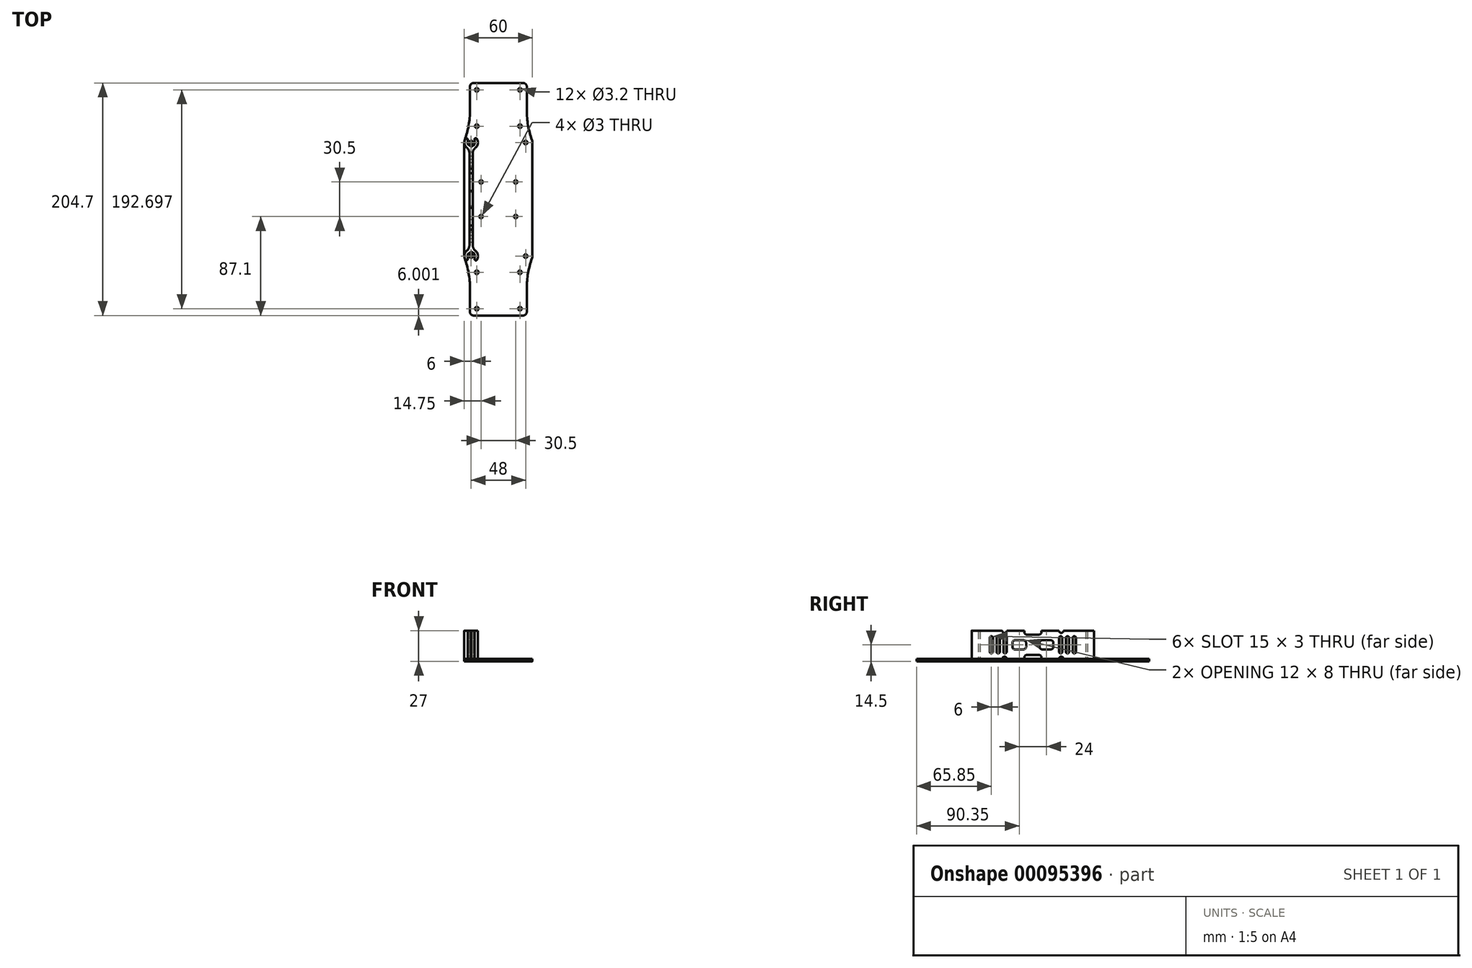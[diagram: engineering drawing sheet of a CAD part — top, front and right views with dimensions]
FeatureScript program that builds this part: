
annotation { "Feature Type Name" : "Feature", "Feature Type Description" : "" }
export const myFeature = defineFeature(function(context is Context, id is Id, definition is map)
    precondition{}
    {
        {
            var Q0;
            Q0=qCreatedBy(makeId("Top.planeOp"),FACE);
            var sketch = newSketch(context, id + "F0", { "sketchPlane" : qUnion([Q0])});
            skLineSegment(sketch, "E0", {"start": v(0, 102.35) * mm, "end": v(-22, 102.35) * mm});
            skLineSegment(sketch, "E1", {"start": v(-25, 99.35) * mm, "end": v(-25, 78.35) * mm});
            skLineSegment(sketch, "E2", {"start": v(-22, -102.35) * mm, "end": v(0, -102.35) * mm});
            skArc(sketch, "E3.filletArc", {"start": v(-22, 102.35) * mm, "mid": v(-24.12, 101.47) * mm, "end": v(-25, 99.35) * mm});
            skArc(sketch, "E4.filletArc", {"start": v(-25, -99.35) * mm, "mid": v(-24.12, -101.47) * mm, "end": v(-22, -102.35) * mm});
            skArc(sketch, "E5.filletArc", {"start": v(-29.64, 52.05) * mm, "mid": v(-29.9, 51.04) * mm, "end": v(-30, 50) * mm});
            skArc(sketch, "E6.MirrorCS", {"start": v(-29.64, -52.05) * mm, "mid": v(-29.9, -51.04) * mm, "end": v(-30, -50) * mm});
            skLineSegment(sketch, "E7.trimOffspring", {"start": v(-25, -78.35) * mm, "end": v(-25, -99.35) * mm});
            skArc(sketch, "E8", {"start": v(-25, -78.35) * mm, "mid": v(-26.17, -65) * mm, "end": v(-29.64, -52.05) * mm});
            skArc(sketch, "E9", {"start": v(-29.64, 52.05) * mm, "mid": v(-26.17, 65) * mm, "end": v(-25, 78.35) * mm});
            skCircle(sketch, "E10", {"center": v(0, 0) * mm, "radius": 125 * mm, "construction": true});
            skLineSegment(sketch, "E11", {"start": v(-95.76, 80.35) * mm, "end": v(95.76, -80.35) * mm, "construction": true});
            skLineSegment(sketch, "E12", {"start": v(95.76, 80.35) * mm, "end": v(-95.76, -80.35) * mm, "construction": true});
            skLineSegment(sketch, "E13", {"start": v(0, 125) * mm, "end": v(0, -125) * mm, "construction": true});
            skLineSegment(sketch, "E14", {"start": v(-95.76, 80.35) * mm, "end": v(95.76, 80.35) * mm, "construction": true});
            skLineSegment(sketch, "E15", {"start": v(-95.76, -80.35) * mm, "end": v(95.76, -80.35) * mm, "construction": true});
            skLineSegment(sketch, "E16", {"start": v(-30, 50) * mm, "end": v(-30, -50) * mm});
            skLineSegment(sketch, "E17.MirrorCS", {"start": v(0, 102.35) * mm, "end": v(22, 102.35) * mm});
            skArc(sketch, "E18.MirrorCS", {"start": v(22, 102.35) * mm, "mid": v(24.12, 101.47) * mm, "end": v(25, 99.35) * mm});
            skLineSegment(sketch, "E19.MirrorCS", {"start": v(25, 99.35) * mm, "end": v(25, 78.35) * mm});
            skArc(sketch, "E20.MirrorCS", {"start": v(29.64, 52.05) * mm, "mid": v(26.17, 65) * mm, "end": v(25, 78.35) * mm});
            skArc(sketch, "E21.MirrorCS", {"start": v(29.64, 52.05) * mm, "mid": v(29.9, 51.04) * mm, "end": v(30, 50) * mm});
            skLineSegment(sketch, "E22.MirrorCS", {"start": v(30, 50) * mm, "end": v(30, -50) * mm});
            skArc(sketch, "E23.MirrorCS", {"start": v(29.64, -52.05) * mm, "mid": v(29.9, -51.04) * mm, "end": v(30, -50) * mm});
            skArc(sketch, "E24.MirrorCS", {"start": v(25, -78.35) * mm, "mid": v(26.17, -65) * mm, "end": v(29.64, -52.05) * mm});
            skArc(sketch, "E25.MirrorCS", {"start": v(25, -99.35) * mm, "mid": v(24.12, -101.47) * mm, "end": v(22, -102.35) * mm});
            skLineSegment(sketch, "E26.MirrorCS", {"start": v(22, -102.35) * mm, "end": v(0, -102.35) * mm});
            skLineSegment(sketch, "E27.MirrorCS", {"start": v(25, -78.35) * mm, "end": v(25, -99.35) * mm});
            skSolve(sketch);
        }
        {
            var Q0;
            Q0=qSketchRegion(id+"F0",true);
            extrude(context, id + "F1", {"entities" : qUnion([Q0]), "oppositeDirection" : true, "depth" : 2 * mm});
        }
        {
            var Q0;
            Q0=makeQuery(id+"F1.opExtrude","CAP_FACE",FACE,{"disambiguationData":[OSD([sQuery(id+"F0.wireOp",EDGE,"E0"),sQuery(id+"F0.wireOp",EDGE,"E1"),sQuery(id+"F0.wireOp",EDGE,"E2"),sQuery(id+"F0.wireOp",EDGE,"E3.filletArc"),sQuery(id+"F0.wireOp",EDGE,"E4.filletArc"),sQuery(id+"F0.wireOp",EDGE,"d22b67ea-32aa-4b1a-bfbd-94ae52c1f5b30.MirrorCS"),sQuery(id+"F0.wireOp",EDGE,"d22b67ea-32aa-4b1a-bfbd-94ae52c1f5b31.MirrorCS"),sQuery(id+"F0.wireOp",EDGE,"d22b67ea-32aa-4b1a-bfbd-94ae52c1f5b32.MirrorCS"),sQuery(id+"F0.wireOp",EDGE,"d22b67ea-32aa-4b1a-bfbd-94ae52c1f5b33.MirrorCS"),sQuery(id+"F0.wireOp",EDGE,"d22b67ea-32aa-4b1a-bfbd-94ae52c1f5b34.MirrorCS")])],"isStart":true});
            var sketch = newSketch(context, id + "F2", { "sketchPlane" : qUnion([Q0])});
            skCircle(sketch, "E28", {"center": v(-19, 96.35) * mm, "radius": 1.6 * mm});
            skCircle(sketch, "E29", {"center": v(-19, 64.35) * mm, "radius": 1.6 * mm});
            skCircle(sketch, "E30", {"center": v(-19, -96.35) * mm, "radius": 1.6 * mm});
            skCircle(sketch, "E31", {"center": v(-19, -64.35) * mm, "radius": 1.6 * mm});
            skCircle(sketch, "E32", {"center": v(-24, -50) * mm, "radius": 1.6 * mm});
            skCircle(sketch, "E33", {"center": v(-24, 50) * mm, "radius": 1.6 * mm});
            skLineSegment(sketch, "E34", {"start": v(-19, 96.35) * mm, "end": v(-19, -96.35) * mm, "construction": true});
            skCircle(sketch, "E35.MirrorC", {"center": v(19, 96.35) * mm, "radius": 1.6 * mm});
            skCircle(sketch, "E36.MirrorC", {"center": v(19, 64.35) * mm, "radius": 1.6 * mm});
            skCircle(sketch, "E37.MirrorC", {"center": v(24, 50) * mm, "radius": 1.6 * mm});
            skCircle(sketch, "E38.MirrorC", {"center": v(24, -50) * mm, "radius": 1.6 * mm});
            skCircle(sketch, "E39.MirrorC", {"center": v(19, -64.35) * mm, "radius": 1.6 * mm});
            skCircle(sketch, "E40.MirrorC", {"center": v(19, -96.35) * mm, "radius": 1.6 * mm});
            skLineSegment(sketch, "E41", {"start": v(-15.25, 15.25) * mm, "end": v(-15.25, -15.25) * mm, "construction": true});
            skPoint(sketch, "E42", {"position": v(-15.25, 0) * mm});
            skLineSegment(sketch, "E43", {"start": v(0, 0) * mm, "end": v(-30, 0) * mm, "construction": true});
            skCircle(sketch, "E44", {"center": v(-15.25, -15.25) * mm, "radius": 1.5 * mm});
            skCircle(sketch, "E45", {"center": v(-15.25, 15.25) * mm, "radius": 1.5 * mm});
            skCircle(sketch, "E46.MirrorC", {"center": v(15.25, 15.25) * mm, "radius": 1.5 * mm});
            skCircle(sketch, "E47.MirrorC", {"center": v(15.25, -15.25) * mm, "radius": 1.5 * mm});
            skSolve(sketch);
        }
        {
            var Q0;
            Q0=qSketchRegion(id+"F2",true);
            extrude(context, id + "F3", {"entities" : qUnion([Q0]), "operationType" : NewBodyOperationType.REMOVE, "endBound" : BoundingType.THROUGH_ALL, "oppositeDirection" : true, "depth" : 25.4 * mm});
        }
        {
            var Q0;
            Q0=qCreatedBy(makeId("Top.planeOp"),FACE);
            var sketch = newSketch(context, id + "F4", { "sketchPlane" : qUnion([Q0])});
            skCircle(sketch, "E48.cCircle", {"center": v(-24, 50) * mm, "radius": 3.1 * mm, "construction": true});
            skLineSegment(sketch, "E48.0", {"start": v(-24, 53.58) * mm, "end": v(-20.9, 51.79) * mm, "construction": true});
            skLineSegment(sketch, "E48.1", {"start": v(-20.9, 51.79) * mm, "end": v(-20.9, 48.21) * mm});
            skLineSegment(sketch, "E48.2", {"start": v(-20.9, 48.21) * mm, "end": v(-24, 46.42) * mm});
            skLineSegment(sketch, "E48.3", {"start": v(-24, 46.42) * mm, "end": v(-27.1, 48.21) * mm});
            skLineSegment(sketch, "E48.4", {"start": v(-27.1, 48.21) * mm, "end": v(-27.1, 51.79) * mm});
            skLineSegment(sketch, "E48.5", {"start": v(-27.1, 51.79) * mm, "end": v(-24, 53.58) * mm, "construction": true});
            skPoint(sketch, "E48.0.midPoint", {"position": v(-22.45, 52.68) * mm});
            skArc(sketch, "E49", {"start": v(-20.25, 45.32) * mm, "mid": v(-18.06, 49.14) * mm, "end": v(-19.08, 53.43) * mm});
            skArc(sketch, "E50", {"start": v(-27.75, -45.32) * mm, "mid": v(-29.94, -49.14) * mm, "end": v(-28.92, -53.43) * mm});
            skLineSegment(sketch, "E51", {"start": v(-25.5, 40.63) * mm, "end": v(-25.5, -40.63) * mm});
            skLineSegment(sketch, "E52", {"start": v(-22.5, 40.63) * mm, "end": v(-22.5, -40.63) * mm});
            skPoint(sketch, "E53.visualSharp", {"position": v(-25.5, 44.2) * mm});
            skArc(sketch, "E53.filletArc", {"start": v(-25.5, 40.63) * mm, "mid": v(-26.1, 43.23) * mm, "end": v(-27.75, 45.32) * mm});
            skPoint(sketch, "E54.visualSharp", {"position": v(-22.5, 44.2) * mm});
            skArc(sketch, "E54.filletArc", {"start": v(-20.25, 45.32) * mm, "mid": v(-21.9, 43.23) * mm, "end": v(-22.5, 40.63) * mm});
            skPoint(sketch, "E55.visualSharp", {"position": v(-22.5, -44.2) * mm});
            skArc(sketch, "E55.filletArc", {"start": v(-22.5, -40.63) * mm, "mid": v(-21.9, -43.23) * mm, "end": v(-20.25, -45.32) * mm});
            skPoint(sketch, "E56.visualSharp", {"position": v(-25.5, -44.2) * mm});
            skArc(sketch, "E56.filletArc", {"start": v(-27.75, -45.32) * mm, "mid": v(-26.1, -43.23) * mm, "end": v(-25.5, -40.63) * mm});
            skLineSegment(sketch, "E57", {"start": v(-24, 50) * mm, "end": v(-24, -50) * mm, "construction": true});
            skCircle(sketch, "E58.cCircle", {"center": v(-24, -50) * mm, "radius": 3.1 * mm, "construction": true});
            skLineSegment(sketch, "E58.0", {"start": v(-24, -46.42) * mm, "end": v(-20.9, -48.21) * mm});
            skLineSegment(sketch, "E58.1", {"start": v(-20.9, -48.21) * mm, "end": v(-20.9, -51.79) * mm});
            skLineSegment(sketch, "E58.2", {"start": v(-20.9, -51.79) * mm, "end": v(-24, -53.58) * mm, "construction": true});
            skLineSegment(sketch, "E58.3", {"start": v(-24, -53.58) * mm, "end": v(-27.1, -51.79) * mm, "construction": true});
            skLineSegment(sketch, "E58.4", {"start": v(-27.1, -51.79) * mm, "end": v(-27.1, -48.21) * mm});
            skLineSegment(sketch, "E58.5", {"start": v(-27.1, -48.21) * mm, "end": v(-24, -46.42) * mm});
            skPoint(sketch, "E58.0.midPoint", {"position": v(-22.45, -47.32) * mm});
            skLineSegment(sketch, "E59", {"start": v(-27.1, -51.79) * mm, "end": v(-27.1, -52.86) * mm});
            skLineSegment(sketch, "E60", {"start": v(-20.9, -51.79) * mm, "end": v(-20.9, -52.86) * mm});
            skArc(sketch, "E61.trimOffspring", {"start": v(-19.08, -53.43) * mm, "mid": v(-18.06, -49.14) * mm, "end": v(-20.25, -45.32) * mm});
            skPoint(sketch, "E62.visualSharp", {"position": v(-27.1, -55.14) * mm});
            skArc(sketch, "E62.filletArc", {"start": v(-28.92, -53.43) * mm, "mid": v(-27.8, -53.82) * mm, "end": v(-27.1, -52.86) * mm});
            skPoint(sketch, "E63.visualSharp", {"position": v(-20.9, -55.14) * mm});
            skArc(sketch, "E63.filletArc", {"start": v(-20.9, -52.86) * mm, "mid": v(-20.2, -53.82) * mm, "end": v(-19.08, -53.43) * mm});
            skLineSegment(sketch, "E64", {"start": v(-27.1, 51.79) * mm, "end": v(-27.1, 52.86) * mm});
            skLineSegment(sketch, "E65", {"start": v(-20.9, 51.79) * mm, "end": v(-20.9, 52.86) * mm});
            skArc(sketch, "E66.trimOffspring", {"start": v(-28.92, 53.43) * mm, "mid": v(-29.94, 49.14) * mm, "end": v(-27.75, 45.32) * mm});
            skPoint(sketch, "E67.visualSharp", {"position": v(-27.1, 55.14) * mm});
            skArc(sketch, "E67.filletArc", {"start": v(-27.1, 52.86) * mm, "mid": v(-27.8, 53.82) * mm, "end": v(-28.92, 53.43) * mm});
            skPoint(sketch, "E68.visualSharp", {"position": v(-20.9, 55.14) * mm});
            skArc(sketch, "E68.filletArc", {"start": v(-19.08, 53.43) * mm, "mid": v(-20.2, 53.82) * mm, "end": v(-20.9, 52.86) * mm});
            skSolve(sketch);
        }
        {
            var Q0;
            Q0=qSketchRegion(id+"F4",true);
            extrude(context, id + "F5", {"entities" : qUnion([Q0]), "depth" : 25 * mm});
        }
        {
            var Q0;
            Q0=makeQuery(id+"F5.opExtrude","SWEPT_FACE",FACE,{"disambiguationData":[OSD([sQuery(id+"F4.wireOp",EDGE,"E51")])]});
            var sketch = newSketch(context, id + "F6", { "sketchPlane" : qUnion([Q0])});
            skLineSegment(sketch, "E69", {"start": v(-21.13, 12.5) * mm, "end": v(21.13, 12.5) * mm, "construction": true});
            skLineSegment(sketch, "E70.bottom", {"start": v(-8, 16.5) * mm, "end": v(-16, 16.5) * mm});
            skLineSegment(sketch, "E70.top", {"start": v(-8, 8.5) * mm, "end": v(-16, 8.5) * mm});
            skLineSegment(sketch, "E70.left", {"start": v(-6, 14.5) * mm, "end": v(-6, 10.5) * mm});
            skLineSegment(sketch, "E70.right", {"start": v(-18, 14.5) * mm, "end": v(-18, 10.5) * mm});
            skPoint(sketch, "E70.middle", {"position": v(-12, 12.5) * mm});
            skPoint(sketch, "E71.visualSharp", {"position": v(-18, 16.5) * mm});
            skArc(sketch, "E71.filletArc", {"start": v(-16, 16.5) * mm, "mid": v(-17.41, 15.91) * mm, "end": v(-18, 14.5) * mm});
            skPoint(sketch, "E72.visualSharp", {"position": v(-18, 8.5) * mm});
            skArc(sketch, "E72.filletArc", {"start": v(-18, 10.5) * mm, "mid": v(-17.41, 9.09) * mm, "end": v(-16, 8.5) * mm});
            skPoint(sketch, "E73.visualSharp", {"position": v(-6, 8.5) * mm});
            skArc(sketch, "E73.filletArc", {"start": v(-8, 8.5) * mm, "mid": v(-6.59, 9.09) * mm, "end": v(-6, 10.5) * mm});
            skPoint(sketch, "E74.visualSharp", {"position": v(-6, 16.5) * mm});
            skArc(sketch, "E74.filletArc", {"start": v(-6, 14.5) * mm, "mid": v(-6.59, 15.91) * mm, "end": v(-8, 16.5) * mm});
            skLineSegment(sketch, "E75.bottom", {"start": v(-7.5, 0) * mm, "end": v(7.5, 0) * mm});
            skLineSegment(sketch, "E75.top", {"start": v(-5.5, 3.5) * mm, "end": v(5.5, 3.5) * mm});
            skLineSegment(sketch, "E75.left", {"start": v(-7.5, 0) * mm, "end": v(-7.5, 1.5) * mm});
            skLineSegment(sketch, "E75.right", {"start": v(7.5, 0) * mm, "end": v(7.5, 1.5) * mm});
            skPoint(sketch, "E76.visualSharp", {"position": v(-7.5, 3.5) * mm});
            skArc(sketch, "E76.filletArc", {"start": v(-5.5, 3.5) * mm, "mid": v(-6.91, 2.91) * mm, "end": v(-7.5, 1.5) * mm});
            skPoint(sketch, "E77.visualSharp", {"position": v(7.5, 3.5) * mm});
            skArc(sketch, "E77.filletArc", {"start": v(7.5, 1.5) * mm, "mid": v(6.91, 2.91) * mm, "end": v(5.5, 3.5) * mm});
            skArc(sketch, "E78", {"start": v(-27, 25) * mm, "mid": v(-25, 23) * mm, "end": v(-23, 25) * mm});
            skLineSegment(sketch, "E79", {"start": v(-25, 25) * mm, "end": v(-25, 0) * mm, "construction": true});
            skArc(sketch, "E80", {"start": v(-23, 0) * mm, "mid": v(-25, 2) * mm, "end": v(-27, 0) * mm});
            skLineSegment(sketch, "E81", {"start": v(-27, 25) * mm, "end": v(-23, 25) * mm});
            skLineSegment(sketch, "E82", {"start": v(-27, 0) * mm, "end": v(-23, 0) * mm});
            skLineSegment(sketch, "E83", {"start": v(0, 25) * mm, "end": v(0, 0) * mm, "construction": true});
            skPoint(sketch, "E84", {"position": v(0, 12.5) * mm});
            skArc(sketch, "E85.MirrorCS", {"start": v(8, 8.5) * mm, "mid": v(6.59, 9.09) * mm, "end": v(6, 10.5) * mm});
            skArc(sketch, "E86.MirrorCS", {"start": v(6, 14.5) * mm, "mid": v(6.59, 15.91) * mm, "end": v(8, 16.5) * mm});
            skArc(sketch, "E87.MirrorCS", {"start": v(18, 10.5) * mm, "mid": v(17.41, 9.09) * mm, "end": v(16, 8.5) * mm});
            skArc(sketch, "E88.MirrorCS", {"start": v(16, 16.5) * mm, "mid": v(17.41, 15.91) * mm, "end": v(18, 14.5) * mm});
            skPoint(sketch, "E89.MirrorP", {"position": v(6, 16.5) * mm});
            skLineSegment(sketch, "E90.MirrorCS", {"start": v(18, 14.5) * mm, "end": v(18, 10.5) * mm});
            skLineSegment(sketch, "E91.MirrorCS", {"start": v(6, 14.5) * mm, "end": v(6, 10.5) * mm});
            skLineSegment(sketch, "E92.MirrorCS", {"start": v(8, 16.5) * mm, "end": v(16, 16.5) * mm});
            skLineSegment(sketch, "E93.MirrorCS", {"start": v(8, 8.5) * mm, "end": v(16, 8.5) * mm});
            skPoint(sketch, "E94.MirrorP", {"position": v(18, 8.5) * mm});
            skPoint(sketch, "E95.MirrorP", {"position": v(12, 12.5) * mm});
            skPoint(sketch, "E96.MirrorP", {"position": v(18, 16.5) * mm});
            skPoint(sketch, "E97.MirrorP", {"position": v(6, 8.5) * mm});
            skLineSegment(sketch, "E98.MirrorCS", {"start": v(27, 25) * mm, "end": v(23, 25) * mm});
            skLineSegment(sketch, "E99.MirrorCS", {"start": v(25, 25) * mm, "end": v(25, 0) * mm, "construction": true});
            skArc(sketch, "E100.MirrorCS", {"start": v(27, 25) * mm, "mid": v(25, 23) * mm, "end": v(23, 25) * mm});
            skLineSegment(sketch, "E101.MirrorCS", {"start": v(27, 0) * mm, "end": v(23, 0) * mm});
            skArc(sketch, "E102.MirrorCS", {"start": v(23, 0) * mm, "mid": v(25, 2) * mm, "end": v(27, 0) * mm});
            skArc(sketch, "E103.MirrorCS", {"start": v(-5.5, 21.5) * mm, "mid": v(-6.91, 22.09) * mm, "end": v(-7.5, 23.5) * mm});
            skArc(sketch, "E104.MirrorCS", {"start": v(7.5, 23.5) * mm, "mid": v(6.91, 22.09) * mm, "end": v(5.5, 21.5) * mm});
            skPoint(sketch, "E105.MirrorP", {"position": v(-7.5, 21.5) * mm});
            skLineSegment(sketch, "E106.MirrorCS", {"start": v(-5.5, 21.5) * mm, "end": v(5.5, 21.5) * mm});
            skLineSegment(sketch, "E107.MirrorCS", {"start": v(-7.5, 25) * mm, "end": v(-7.5, 23.5) * mm});
            skPoint(sketch, "E108.MirrorP", {"position": v(7.5, 21.5) * mm});
            skLineSegment(sketch, "E109.MirrorCS", {"start": v(7.5, 25) * mm, "end": v(7.5, 23.5) * mm});
            skLineSegment(sketch, "E110.MirrorCS", {"start": v(-7.5, 25) * mm, "end": v(7.5, 25) * mm});
            skLineSegment(sketch, "E111", {"start": v(-38, 18.5) * mm, "end": v(-16.95, 18.5) * mm, "construction": true});
            skLineSegment(sketch, "E112", {"start": v(-38, 6.5) * mm, "end": v(-16.95, 6.5) * mm, "construction": true});
            skLineSegment(sketch, "E113.left", {"start": v(-38, 6.5) * mm, "end": v(-38, 18.5) * mm});
            skLineSegment(sketch, "E113.right", {"start": v(-35, 6.5) * mm, "end": v(-35, 18.5) * mm});
            skArc(sketch, "E114", {"start": v(-35, 18.5) * mm, "mid": v(-36.5, 20) * mm, "end": v(-38, 18.5) * mm});
            skArc(sketch, "E115", {"start": v(-38, 6.5) * mm, "mid": v(-36.5, 5) * mm, "end": v(-35, 6.5) * mm});
            skLineSegment(sketch, "E116.1.0.0", {"start": v(-29, 6.5) * mm, "end": v(-29, 18.5) * mm});
            skArc(sketch, "E116.1.0.1", {"start": v(-32, 6.5) * mm, "mid": v(-30.5, 5) * mm, "end": v(-29, 6.5) * mm});
            skArc(sketch, "E116.1.0.2", {"start": v(-29, 18.5) * mm, "mid": v(-30.5, 20) * mm, "end": v(-32, 18.5) * mm});
            skLineSegment(sketch, "E116.1.0.3", {"start": v(-32, 6.5) * mm, "end": v(-32, 18.5) * mm});
            skLineSegment(sketch, "E116.2.0.0", {"start": v(-23, 6.5) * mm, "end": v(-23, 18.5) * mm});
            skArc(sketch, "E116.2.0.1", {"start": v(-26, 6.5) * mm, "mid": v(-24.5, 5) * mm, "end": v(-23, 6.5) * mm});
            skArc(sketch, "E116.2.0.2", {"start": v(-23, 18.5) * mm, "mid": v(-24.5, 20) * mm, "end": v(-26, 18.5) * mm});
            skLineSegment(sketch, "E116.2.0.3", {"start": v(-26, 6.5) * mm, "end": v(-26, 18.5) * mm});
            skLineSegment(sketch, "E116.direction1", {"start": v(-35, 6.5) * mm, "end": v(-29, 6.5) * mm, "construction": true});
            skArc(sketch, "E117.MirrorCS", {"start": v(32, 6.5) * mm, "mid": v(30.5, 5) * mm, "end": v(29, 6.5) * mm});
            skLineSegment(sketch, "E118.MirrorCS", {"start": v(38, 6.5) * mm, "end": v(38, 18.5) * mm});
            skArc(sketch, "E119.MirrorCS", {"start": v(26, 6.5) * mm, "mid": v(24.5, 5) * mm, "end": v(23, 6.5) * mm});
            skLineSegment(sketch, "E120.MirrorCS", {"start": v(35, 6.5) * mm, "end": v(35, 18.5) * mm});
            skLineSegment(sketch, "E121.MirrorCS", {"start": v(23, 6.5) * mm, "end": v(23, 18.5) * mm});
            skLineSegment(sketch, "E122.MirrorCS", {"start": v(29, 6.5) * mm, "end": v(29, 18.5) * mm});
            skArc(sketch, "E123.MirrorCS", {"start": v(23, 18.5) * mm, "mid": v(24.5, 20) * mm, "end": v(26, 18.5) * mm});
            skArc(sketch, "E124.MirrorCS", {"start": v(29, 18.5) * mm, "mid": v(30.5, 20) * mm, "end": v(32, 18.5) * mm});
            skArc(sketch, "E125.MirrorCS", {"start": v(35, 18.5) * mm, "mid": v(36.5, 20) * mm, "end": v(38, 18.5) * mm});
            skLineSegment(sketch, "E126.MirrorCS", {"start": v(26, 6.5) * mm, "end": v(26, 18.5) * mm});
            skLineSegment(sketch, "E127.MirrorCS", {"start": v(32, 6.5) * mm, "end": v(32, 18.5) * mm});
            skArc(sketch, "E128.MirrorCS", {"start": v(38, 6.5) * mm, "mid": v(36.5, 5) * mm, "end": v(35, 6.5) * mm});
            skLineSegment(sketch, "E129.MirrorCS", {"start": v(35, 6.5) * mm, "end": v(29, 6.5) * mm, "construction": true});
            skSolve(sketch);
        }
        {
            var Q0;
            Q0=qSketchRegion(id+"F6",true);
            var Q1;
            Q1=makeQuery(id+"F5.opExtrude","SWEPT_FACE",FACE,{"disambiguationData":[OSD([sQuery(id+"F4.wireOp",EDGE,"E52")])]});
            extrude(context, id + "F7", {"entities" : qUnion([Q0]), "operationType" : NewBodyOperationType.REMOVE, "endBound" : BoundingType.UP_TO_SURFACE, "oppositeDirection" : true, "endBoundEntityFace" : qUnion([Q1]), "depth" : 25 * mm});
        }
        {
            var Q0;
            Q0=qCreatedBy(makeId("Top.planeOp"),FACE);
            cPlane(context, id + "F8", {"entities" : qUnion([Q0]), "cplaneType" : CPlaneType.OFFSET, "offset" : 12.5 * mm, "width" : 150 * mm, "height" : 150 * mm});
        }
        {
            var Q0;
            Q0=qCreatedBy(id+"F8.planeOp",FACE);
            var sketch = newSketch(context, id + "F9", { "sketchPlane" : qUnion([Q0])});
            skLineSegment(sketch, "E130", {"start": v(-26.25, 21.25) * mm, "end": v(-26.25, 19.75) * mm});
            skLineSegment(sketch, "E131", {"start": v(-25.75, 19.25) * mm, "end": v(-19.25, 19.25) * mm});
            skLineSegment(sketch, "E132", {"start": v(-19.25, 19.25) * mm, "end": v(-18.25, 18.25) * mm});
            skLineSegment(sketch, "E133", {"start": v(-18.25, 18.25) * mm, "end": v(-15.25, 18.25) * mm});
            skLineSegment(sketch, "E134", {"start": v(-6.48, 15.25) * mm, "end": v(-35.06, 15.25) * mm, "construction": true});
            skArc(sketch, "E135", {"start": v(-12.25, 15.25) * mm, "mid": v(-13.13, 17.37) * mm, "end": v(-15.25, 18.25) * mm});
            skLineSegment(sketch, "E136", {"start": v(-26.25, 21.25) * mm, "end": v(-27.75, 21.25) * mm});
            skLineSegment(sketch, "E137", {"start": v(-27.75, 21.25) * mm, "end": v(-27.75, 15.25) * mm});
            skPoint(sketch, "E138.visualSharp", {"position": v(-26.25, 19.25) * mm});
            skArc(sketch, "E138.filletArc", {"start": v(-26.25, 19.75) * mm, "mid": v(-26.1, 19.4) * mm, "end": v(-25.75, 19.25) * mm});
            skLineSegment(sketch, "E139.MirrorCS", {"start": v(-27.75, 9.25) * mm, "end": v(-27.75, 15.25) * mm});
            skLineSegment(sketch, "E140.MirrorCS", {"start": v(-26.25, 9.25) * mm, "end": v(-27.75, 9.25) * mm});
            skLineSegment(sketch, "E141.MirrorCS", {"start": v(-26.25, 9.25) * mm, "end": v(-26.25, 10.75) * mm});
            skArc(sketch, "E142.MirrorCS", {"start": v(-26.25, 10.75) * mm, "mid": v(-26.1, 11.1) * mm, "end": v(-25.75, 11.25) * mm});
            skLineSegment(sketch, "E143.MirrorCS", {"start": v(-25.75, 11.25) * mm, "end": v(-19.25, 11.25) * mm});
            skLineSegment(sketch, "E144.MirrorCS", {"start": v(-19.25, 11.25) * mm, "end": v(-18.25, 12.25) * mm});
            skLineSegment(sketch, "E145.MirrorCS", {"start": v(-18.25, 12.25) * mm, "end": v(-15.25, 12.25) * mm});
            skArc(sketch, "E146.MirrorCS", {"start": v(-12.25, 15.25) * mm, "mid": v(-13.13, 13.13) * mm, "end": v(-15.25, 12.25) * mm});
            skSolve(sketch);
        }
        {
            var Q0;
            Q0=qSketchRegion(id+"F9",true);
            extrude(context, id + "F10", {"entities" : qUnion([Q0]), "endBound" : BoundingType.SYMMETRIC, "depth" : 8 * mm});
        }
        {
            var Q0;
            Q0=makeQuery(id+"F10.opExtrude","CAP_FACE",FACE,{"disambiguationData":[OSD([sQuery(id+"F9.wireOp",EDGE,"E130"),sQuery(id+"F9.wireOp",EDGE,"E131"),sQuery(id+"F9.wireOp",EDGE,"E132"),sQuery(id+"F9.wireOp",EDGE,"E133"),sQuery(id+"F9.wireOp",EDGE,"E135"),sQuery(id+"F9.wireOp",EDGE,"E136"),sQuery(id+"F9.wireOp",EDGE,"E137"),sQuery(id+"F9.wireOp",EDGE,"E138.filletArc"),sQuery(id+"F9.wireOp",EDGE,"E139.MirrorCS"),sQuery(id+"F9.wireOp",EDGE,"E140.MirrorCS"),sQuery(id+"F9.wireOp",EDGE,"E141.MirrorCS"),sQuery(id+"F9.wireOp",EDGE,"E142.MirrorCS"),sQuery(id+"F9.wireOp",EDGE,"E143.MirrorCS"),sQuery(id+"F9.wireOp",EDGE,"E144.MirrorCS"),sQuery(id+"F9.wireOp",EDGE,"E145.MirrorCS"),sQuery(id+"F9.wireOp",EDGE,"E146.MirrorCS")])],"isStart":false});
            var sketch = newSketch(context, id + "F11", { "sketchPlane" : qUnion([Q0])});
            skCircle(sketch, "E147", {"center": v(-15.25, 15.25) * mm, "radius": 1.5 * mm});
            skSolve(sketch);
        }
        {
            var Q0;
            Q0=qSketchRegion(id+"F11",true);
            var Q1;
            Q1=makeQuery(id+"F10.opExtrude","CAP_FACE",FACE,{"disambiguationData":[OSD([sQuery(id+"F9.wireOp",EDGE,"E130"),sQuery(id+"F9.wireOp",EDGE,"E131"),sQuery(id+"F9.wireOp",EDGE,"E132"),sQuery(id+"F9.wireOp",EDGE,"E133"),sQuery(id+"F9.wireOp",EDGE,"E135"),sQuery(id+"F9.wireOp",EDGE,"E136"),sQuery(id+"F9.wireOp",EDGE,"E137"),sQuery(id+"F9.wireOp",EDGE,"E138.filletArc"),sQuery(id+"F9.wireOp",EDGE,"E139.MirrorCS"),sQuery(id+"F9.wireOp",EDGE,"E140.MirrorCS"),sQuery(id+"F9.wireOp",EDGE,"E141.MirrorCS"),sQuery(id+"F9.wireOp",EDGE,"E142.MirrorCS"),sQuery(id+"F9.wireOp",EDGE,"E143.MirrorCS"),sQuery(id+"F9.wireOp",EDGE,"E144.MirrorCS"),sQuery(id+"F9.wireOp",EDGE,"E145.MirrorCS"),sQuery(id+"F9.wireOp",EDGE,"E146.MirrorCS")])],"isStart":true});
            extrude(context, id + "F12", {"entities" : qUnion([Q0]), "operationType" : NewBodyOperationType.REMOVE, "endBound" : BoundingType.UP_TO_SURFACE, "oppositeDirection" : true, "endBoundEntityFace" : qUnion([Q1]), "depth" : 25 * mm});
        }
        {
            var Q0;
            Q0=makeQuery(id+"F10.opExtrude","SWEPT_BODY",BODY,{"disambiguationData":[OSD([sQuery(id+"F9.wireOp",EDGE,"E130"),sQuery(id+"F9.wireOp",EDGE,"E131"),sQuery(id+"F9.wireOp",EDGE,"E132"),sQuery(id+"F9.wireOp",EDGE,"E133"),sQuery(id+"F9.wireOp",EDGE,"E135"),sQuery(id+"F9.wireOp",EDGE,"E136"),sQuery(id+"F9.wireOp",EDGE,"E137"),sQuery(id+"F9.wireOp",EDGE,"E138.filletArc"),sQuery(id+"F9.wireOp",EDGE,"E139.MirrorCS"),sQuery(id+"F9.wireOp",EDGE,"E140.MirrorCS"),sQuery(id+"F9.wireOp",EDGE,"E141.MirrorCS"),sQuery(id+"F9.wireOp",EDGE,"E142.MirrorCS"),sQuery(id+"F9.wireOp",EDGE,"E143.MirrorCS"),sQuery(id+"F9.wireOp",EDGE,"E144.MirrorCS"),sQuery(id+"F9.wireOp",EDGE,"E145.MirrorCS"),sQuery(id+"F9.wireOp",EDGE,"E146.MirrorCS")])]});
            deleteBodies(context, id + "F13", {"entities" : qUnion([Q0])});
        }
    });
